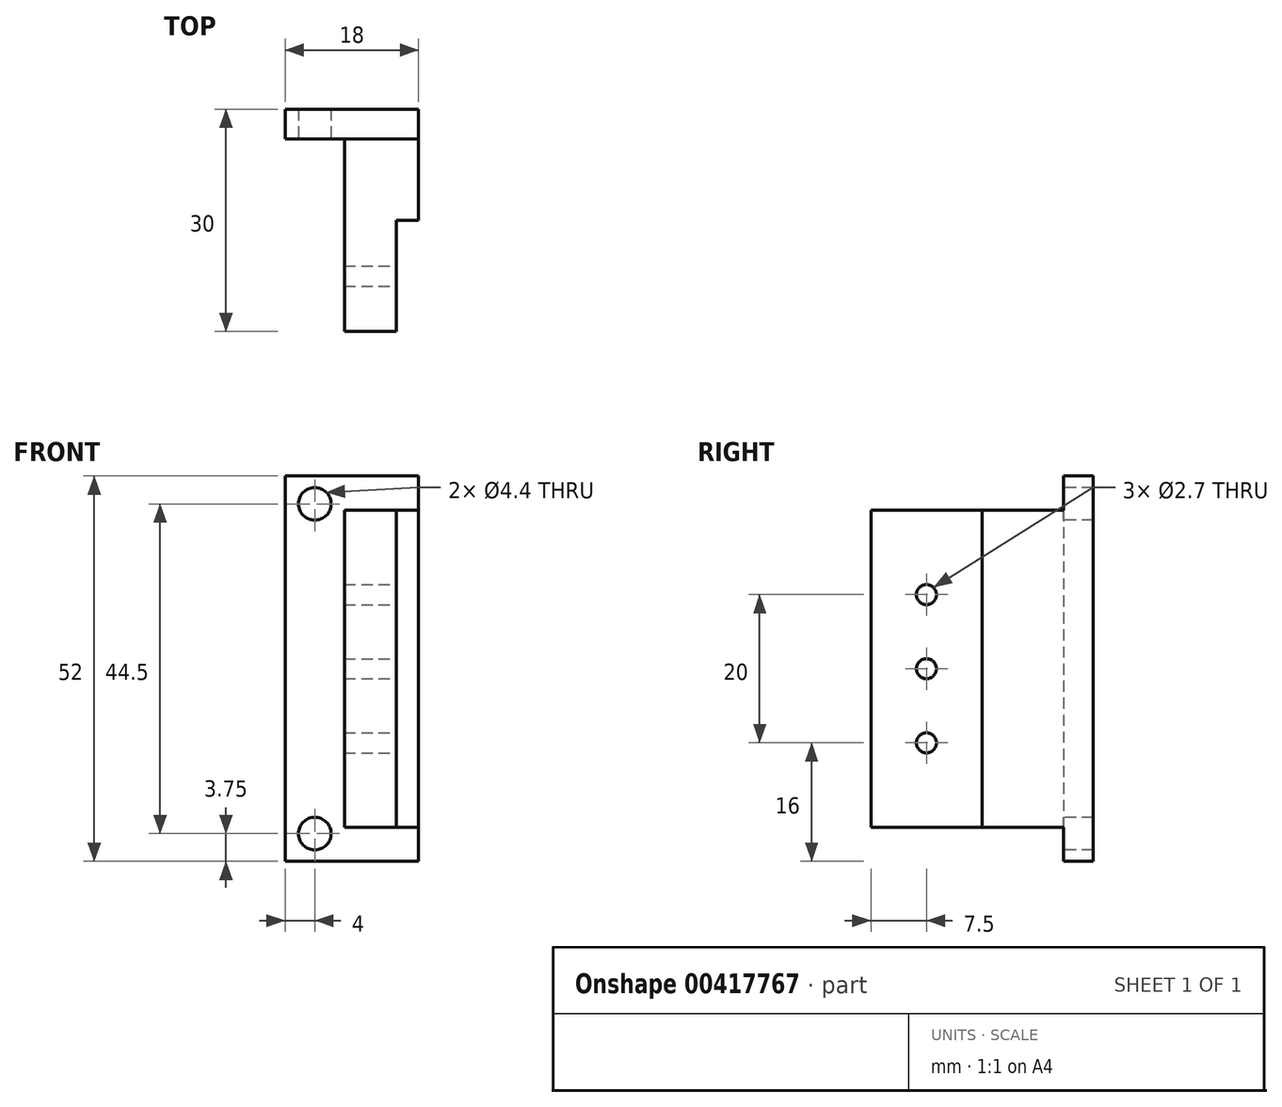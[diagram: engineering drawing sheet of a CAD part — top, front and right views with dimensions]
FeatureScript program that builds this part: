
annotation { "Feature Type Name" : "Feature", "Feature Type Description" : "" }
export const myFeature = defineFeature(function(context is Context, id is Id, definition is map)
    precondition{}
    {
        {
            var Q0;
            Q0=qCreatedBy(makeId("Right.planeOp"),FACE);
            var sketch = newSketch(context, id + "F0", { "sketchPlane" : qUnion([Q0])});
            skLineSegment(sketch, "E0", {"start": v(-23, 0) * mm, "end": v(-23, -42.8) * mm});
            skLineSegment(sketch, "E1", {"start": v(-23, -42.8) * mm, "end": v(0, -42.8) * mm});
            skLineSegment(sketch, "E2", {"start": v(0, -42.8) * mm, "end": v(7, -42.8) * mm});
            skLineSegment(sketch, "E3", {"start": v(7, -42.8) * mm, "end": v(7, 0) * mm});
            skLineSegment(sketch, "E4", {"start": v(7, 0) * mm, "end": v(-23, 0) * mm});
            skSolve(sketch);
        }
        {
            var Q0;
            Q0=qSketchRegion(id+"F0",true);
            extrude(context, id + "F1", {"entities" : qUnion([Q0]), "depth" : 10 * mm});
        }
        {
            var Q0;
            Q0=makeQuery(id+"F1.opExtrude","CAP_FACE",FACE,{"disambiguationData":[OSD([sQuery(id+"F0.wireOp",EDGE,"E0"),sQuery(id+"F0.wireOp",EDGE,"E1"),sQuery(id+"F0.wireOp",EDGE,"atwlfwFM-EWD5-Dq7t-sYPP-BAGUTNfMhWBh"),sQuery(id+"F0.wireOp",EDGE,"AIgXWtW0-bvW5-zazV-hA9D-g2wHTwuUtshl"),sQuery(id+"F0.wireOp",EDGE,"EVCZ9n5H-zkxn-U0ba-5S4D-QnfGiyXXYUrJ"),sQuery(id+"F0.wireOp",EDGE,"E2"),sQuery(id+"F0.wireOp",EDGE,"Q9r14aXl-3uPJ-I0Vw-ov1x-yyKcDtLKnFAO"),sQuery(id+"F0.wireOp",EDGE,"TVkT7qMT-ybPu-MgMp-vtdt-gMsgdEgQD1bz"),sQuery(id+"F0.wireOp",EDGE,"G8zQImhZ-QrOZ-a84S-6XZv-LT9HIZbCM7Fn"),sQuery(id+"F0.wireOp",EDGE,"oWis39jh-Rm85-Uz38-EknD-EUo8zdozpWjd"),sQuery(id+"F0.wireOp",EDGE,"Hnrp3uHZ-qRKS-MQhy-jvpP-tpVSL3Cb9KD8"),sQuery(id+"F0.wireOp",EDGE,"xNTsCDME-N2rM-Kig5-0tdb-CCG1r8GUBbaT"),sQuery(id+"F0.wireOp",EDGE,"E3"),sQuery(id+"F0.wireOp",EDGE,"E4")])],"isStart":false});
            var sketch = newSketch(context, id + "F2", { "sketchPlane" : qUnion([Q0])});
            skLineSegment(sketch, "E5.bottom", {"start": v(-23, 0) * mm, "end": v(-8, 0) * mm});
            skLineSegment(sketch, "E5.top", {"start": v(-23, -42.8) * mm, "end": v(-8, -42.8) * mm});
            skLineSegment(sketch, "E5.left", {"start": v(-23, 0) * mm, "end": v(-23, -42.8) * mm});
            skLineSegment(sketch, "E5.right", {"start": v(-8, 0) * mm, "end": v(-8, -42.8) * mm});
            skSolve(sketch);
        }
        {
            var Q0;
            Q0=qSketchRegion(id+"F2",true);
            extrude(context, id + "F3", {"entities" : qUnion([Q0]), "operationType" : NewBodyOperationType.REMOVE, "oppositeDirection" : true, "depth" : 3 * mm});
        }
        {
            var Q0;
            Q0=makeQuery(id+"F3.boolean.opBoolean","COPY",FACE,{"derivedFrom":makeQuery(id+"F3.opExtrude","CAP_FACE",FACE,{"disambiguationData":[OSD([sQuery(id+"F2.wireOp",EDGE,"E5.bottom"),sQuery(id+"F2.wireOp",EDGE,"E5.top"),sQuery(id+"F2.wireOp",EDGE,"E5.left"),sQuery(id+"F2.wireOp",EDGE,"E5.right")])],"isStart":false})});
            var sketch = newSketch(context, id + "F4", { "sketchPlane" : qUnion([Q0])});
            skLineSegment(sketch, "E6", {"start": v(-15.5, 6.41) * mm, "end": v(-15.5, -51.63) * mm, "construction": true});
            skPoint(sketch, "E6.startSnap0", {"position": v(-15.5, 0) * mm});
            skCircle(sketch, "E7", {"center": v(-15.5, -21.4) * mm, "radius": 1.35 * mm});
            skPoint(sketch, "E7.centerSnap0", {"position": v(-23, -21.4) * mm});
            skCircle(sketch, "E8", {"center": v(-15.5, -11.4) * mm, "radius": 1.35 * mm});
            skCircle(sketch, "E9", {"center": v(-15.5, -31.4) * mm, "radius": 1.35 * mm});
            skSolve(sketch);
        }
        {
            var Q0;
            Q0=qSketchRegion(id+"F4",true);
            extrude(context, id + "F5", {"entities" : qUnion([Q0]), "operationType" : NewBodyOperationType.REMOVE, "endBound" : BoundingType.THROUGH_ALL, "oppositeDirection" : true, "depth" : 25 * mm});
        }
        {
            var Q0;
            Q0=makeQuery(id+"F1.opExtrude","CAP_FACE",FACE,{"disambiguationData":[OSD([sQuery(id+"F0.wireOp",EDGE,"E0"),sQuery(id+"F0.wireOp",EDGE,"E1"),sQuery(id+"F0.wireOp",EDGE,"E2"),sQuery(id+"F0.wireOp",EDGE,"E3"),sQuery(id+"F0.wireOp",EDGE,"E4")])],"isStart":true});
            var sketch = newSketch(context, id + "F6", { "sketchPlane" : qUnion([Q0])});
            skLineSegment(sketch, "E10.bottom", {"start": v(-7, 4.6) * mm, "end": v(-3, 4.6) * mm});
            skLineSegment(sketch, "E10.top", {"start": v(-7, -47.4) * mm, "end": v(-3, -47.4) * mm});
            skLineSegment(sketch, "E10.left", {"start": v(-7, 4.6) * mm, "end": v(-7, -47.4) * mm});
            skLineSegment(sketch, "E10.right", {"start": v(-3, 4.6) * mm, "end": v(-3, -47.4) * mm});
            skLineSegment(sketch, "E11", {"start": v(-16.94, -21.4) * mm, "end": v(40.52, -21.4) * mm, "construction": true});
            skPoint(sketch, "E11.startSnap0", {"position": v(-7, -21.4) * mm});
            skSolve(sketch);
        }
        {
            var Q0;
            {var subQ0=sQuery(id+"F6.wireOp",EDGE,"E10.bottom");Q0=makeQuery(id+"F6.imprint","IMPRINT",FACE,{"disambiguationData":[TD([[makeQuery(id+"F6.imprint","IMPRINT",EDGE,{"derivedFrom":subQ0}),-1.0]])]});}
            var Q1;
            {var subQ0=sQuery(id+"F6.wireOp",EDGE,"E10.top");Q1=makeQuery(id+"F6.imprint","IMPRINT",FACE,{"disambiguationData":[TD([[makeQuery(id+"F6.imprint","IMPRINT",EDGE,{"derivedFrom":subQ0}),1.0]])]});}
            var Q2;
            {var subQ0=sQuery(id+"F6.wireOp",EDGE,"E10.left");var subQ3=makeQuery(id+"F1.opExtrude","CAP_EDGE",EDGE,{"disambiguationData":[OSD([sQuery(id+"F0.wireOp",EDGE,"E4")])],"isStart":true});var subQ4=makeQuery(id+"F6.imprint","INTERSECT",VERTEX,{"derivedFrom":[subQ3,subQ0]});Q2=makeQuery(id+"F6.imprint","IMPRINT",FACE,{"disambiguationData":[TD([[makeQuery(id+"F6.imprint","IMPRINT",EDGE,{"disambiguationData":[TD([[subQ4,-1.0]])],"derivedFrom":subQ3}),-1.0]])]});}
            extrude(context, id + "F7", {"entities" : qUnion([Q0, Q1, Q2]), "operationType" : NewBodyOperationType.ADD, "depth" : 8 * mm});
        }
        {
            var Q0;
            {var subQ0=sQuery(id+"F6.wireOp",EDGE,"E10.top");var subQ4=sQuery(id+"F6.wireOp",EDGE,"E10.left");var subQ5=sQuery(id+"F6.wireOp",EDGE,"E10.right");Q0=makeQuery(id+"F7.boolean.opBoolean","SPLIT",FACE,{"disambiguationData":[TD([makeQuery(id+"F7.opExtrude","SWEPT_FACE",FACE,{"disambiguationData":[OSD([subQ0])]})])],"derivedFrom":makeQuery(id+"F7.opExtrude","CAP_FACE",FACE,{"disambiguationData":[OSD([sQuery(id+"F6.wireOp",EDGE,"E10.bottom"),subQ0,subQ4,subQ5])],"isStart":true})});}
            var Q1;
            {var subQ0=sQuery(id+"F0.wireOp",EDGE,"E4");var subQ1=sQuery(id+"F6.wireOp",EDGE,"E10.right");var subQ3=sQuery(id+"F6.wireOp",EDGE,"E10.left");var subQ4=sQuery(id+"F6.wireOp",EDGE,"E10.bottom");Q1=makeQuery(id+"F7.boolean.opBoolean","SPLIT",FACE,{"disambiguationData":[TD([makeQuery(id+"F1.opExtrude","SWEPT_FACE",FACE,{"disambiguationData":[OSD([subQ0])]})])],"derivedFrom":makeQuery(id+"F7.opExtrude","CAP_FACE",FACE,{"disambiguationData":[OSD([subQ4,sQuery(id+"F6.wireOp",EDGE,"E10.top"),subQ3,subQ1])],"isStart":true})});}
            extrude(context, id + "F8", {"entities" : qUnion([Q0, Q1]), "operationType" : NewBodyOperationType.ADD, "depth" : 10 * mm});
        }
        {
            var Q0;
            {var subQ0=sQuery(id+"F6.wireOp",EDGE,"E10.top");var subQ3=sQuery(id+"F6.wireOp",EDGE,"E10.right");var subQ4=sQuery(id+"F6.wireOp",EDGE,"E10.bottom");var subQ5=makeQuery(id+"F7.opExtrude","CAP_FACE",FACE,{"disambiguationData":[OSD([subQ4,subQ0,sQuery(id+"F6.wireOp",EDGE,"E10.left"),subQ3])],"isStart":true});var subQ6=sQuery(id+"F0.wireOp",EDGE,"E4");var subQ8=makeQuery(id+"F7.opExtrude","SWEPT_FACE",FACE,{"disambiguationData":[OSD([subQ3])]});var subQ9=makeQuery(id+"F7.opExtrude","CAP_EDGE",EDGE,{"disambiguationData":[OSD([subQ3])],"isStart":true});Q0=makeQuery(id+"F8.boolean.opBoolean","MERGE",FACE,{"derivedFrom":[subQ8,makeQuery(id+"F8.opExtrude","SWEPT_FACE",FACE,{"disambiguationData":[OSD([subQ3]),TDD([makeQuery(id+"F7.boolean.opBoolean","SPLIT",EDGE,{"disambiguationData":[topologyDisambiguationEdgeConnected([subQ5,subQ8]),TD([makeQuery(id+"F1.opExtrude","SWEPT_FACE",FACE,{"disambiguationData":[OSD([subQ6])]})])],"derivedFrom":subQ9})])]}),makeQuery(id+"F8.opExtrude","SWEPT_FACE",FACE,{"disambiguationData":[OSD([subQ3]),TDD([makeQuery(id+"F7.boolean.opBoolean","SPLIT",EDGE,{"disambiguationData":[topologyDisambiguationEdgeConnected([subQ5,subQ8]),TD([makeQuery(id+"F7.opExtrude","SWEPT_FACE",FACE,{"disambiguationData":[OSD([subQ0])]})])],"derivedFrom":subQ9})])]})]});}
            var sketch = newSketch(context, id + "F9", { "sketchPlane" : qUnion([Q0])});
            skCircle(sketch, "E12", {"center": v(-4, 0.85) * mm, "radius": 2.2 * mm});
            skCircle(sketch, "E13", {"center": v(-4, -43.65) * mm, "radius": 2.2 * mm});
            skLineSegment(sketch, "E14", {"start": v(-4, 8.8) * mm, "end": v(-4, -54.97) * mm, "construction": true});
            skLineSegment(sketch, "E15", {"start": v(-16.51, -21.4) * mm, "end": v(17.57, -21.4) * mm, "construction": true});
            skPoint(sketch, "E15.startSnap0", {"position": v(-8, -21.4) * mm});
            skSolve(sketch);
        }
        {
            var Q0;
            Q0 = qSketchRegion(id + "F9", true);
            extrude(context, id + "F10", {"entities" : qUnion([Q0]), "operationType" : NewBodyOperationType.REMOVE, "endBound" : BoundingType.THROUGH_ALL, "oppositeDirection" : true, "depth" : 25 * mm});
        }
    });
